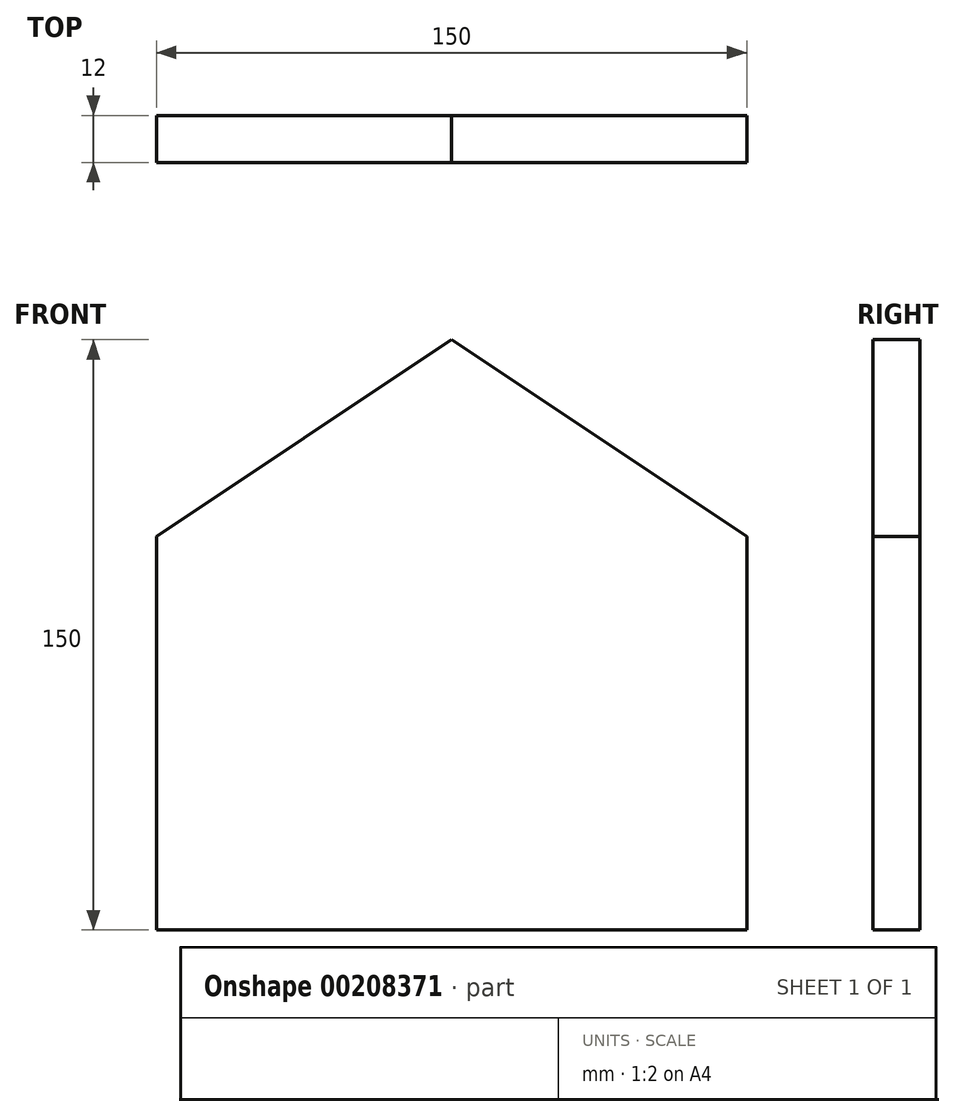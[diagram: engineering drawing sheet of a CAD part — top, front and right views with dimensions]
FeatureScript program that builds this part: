
annotation { "Feature Type Name" : "Feature", "Feature Type Description" : "" }
export const myFeature = defineFeature(function(context is Context, id is Id, definition is map)
    precondition{}
    {
        {
            var Q0;
            Q0=qCreatedBy(makeId("Front.planeOp"),FACE);
            var sketch = newSketch(context, id + "F0", { "sketchPlane" : qUnion([Q0])});
            skLineSegment(sketch, "E0.bottom", {"start": v(-75, 0) * mm, "end": v(75, 0) * mm});
            skLineSegment(sketch, "E0.left", {"start": v(-75, 0) * mm, "end": v(-75, 100) * mm});
            skLineSegment(sketch, "E0.right", {"start": v(75, 0) * mm, "end": v(75, 100) * mm});
            skLineSegment(sketch, "E1", {"start": v(-75, 100) * mm, "end": v(0, 150) * mm});
            skLineSegment(sketch, "E2", {"start": v(0, 150) * mm, "end": v(75, 100) * mm});
            skSolve(sketch);
        }
        {
            var Q0;
            Q0=makeQuery(id+"F0.imprint","IMPRINT",FACE,{"disambiguationData":[TD([[makeQuery(id+"F0.imprint","IMPRINT",EDGE,{"derivedFrom":sQuery(id+"F0.wireOp",EDGE,"E0.bottom")}),1.0]])]});
            extrude(context, id + "F1", {"entities" : qUnion([Q0]), "depth" : 12 * mm});
        }
    });
